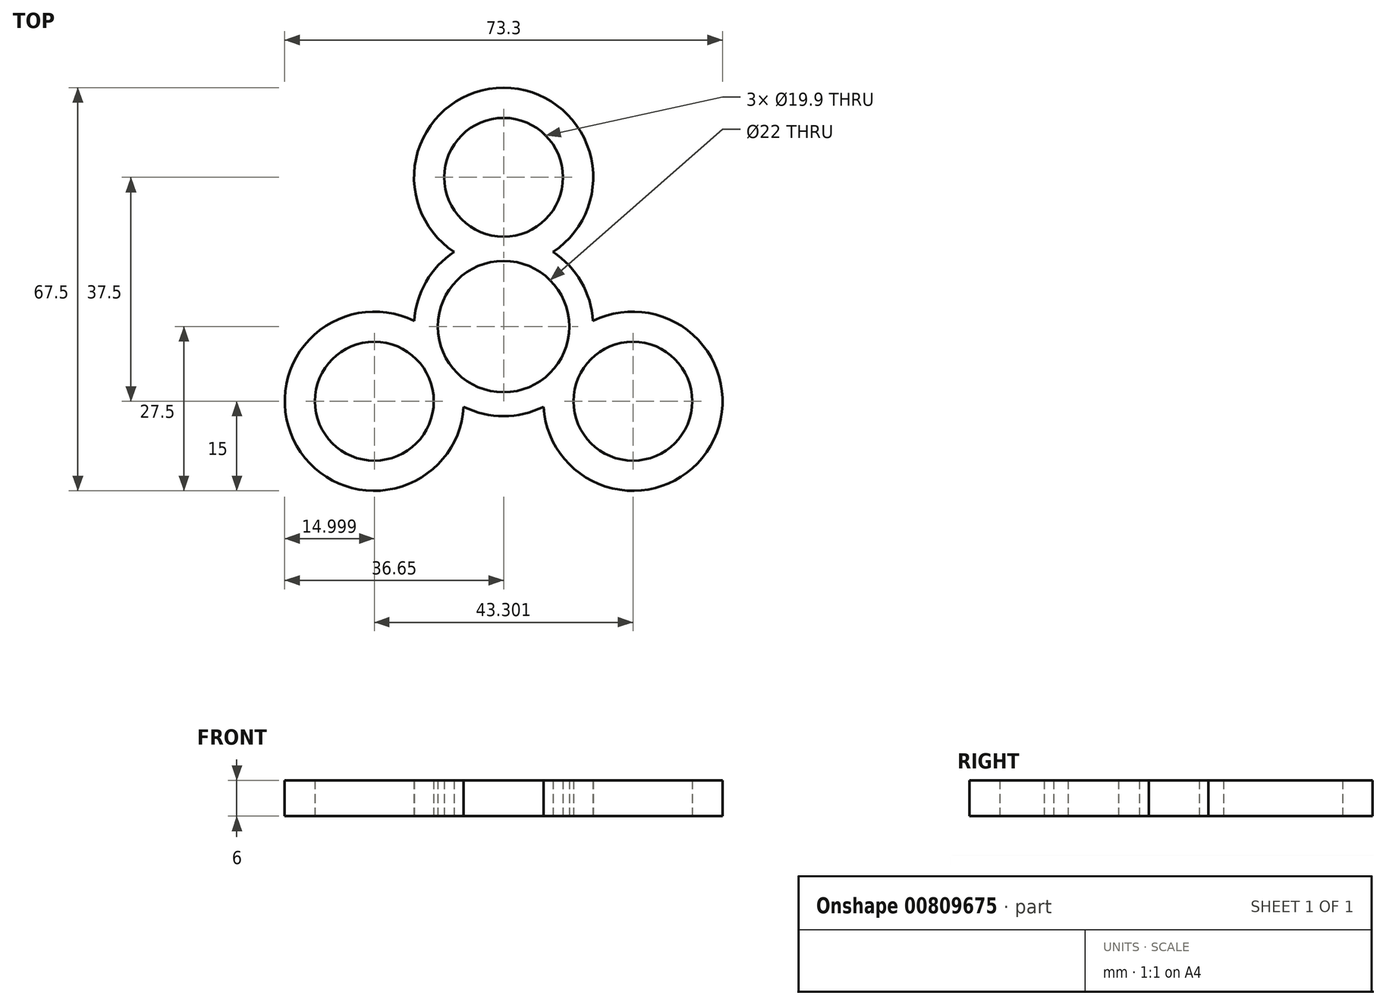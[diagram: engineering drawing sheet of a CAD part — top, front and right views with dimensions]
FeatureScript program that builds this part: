
annotation { "Feature Type Name" : "Feature", "Feature Type Description" : "" }
export const myFeature = defineFeature(function(context is Context, id is Id, definition is map)
    precondition{}
    {
        {
            var Q0;
            Q0=qCreatedBy(makeId("Top.planeOp"),FACE);
            var sketch = newSketch(context, id + "F0", { "sketchPlane" : qUnion([Q0])});
            skArc(sketch, "E0", {"start": v(9.53, 5.5) * mm, "mid": v(0, 11) * mm, "end": v(-9.53, 5.5) * mm});
            skCircle(sketch, "E1", {"center": v(0, 25) * mm, "radius": 9.95 * mm});
            skArc(sketch, "E2", {"start": v(-8.3, 12.5) * mm, "mid": v(-10.93, 10.27) * mm, "end": v(-13, 7.5) * mm});
            skArc(sketch, "E3", {"start": v(8.3, 12.5) * mm, "mid": v(0, 40) * mm, "end": v(-8.3, 12.5) * mm});
            skArc(sketch, "E4.trimOffspring", {"start": v(13, 7.5) * mm, "mid": v(10.93, 10.27) * mm, "end": v(8.3, 12.5) * mm});
            skArc(sketch, "E5.1.0", {"start": v(-14.97, 0.93) * mm, "mid": v(-34.64, -20) * mm, "end": v(-6.68, -13.43) * mm});
            skCircle(sketch, "E5.1.1", {"center": v(-21.65, -12.5) * mm, "radius": 9.95 * mm});
            skArc(sketch, "E5.1.2", {"start": v(-13, 7.5) * mm, "mid": v(-14.36, 4.33) * mm, "end": v(-14.97, 0.93) * mm});
            skArc(sketch, "E5.1.3", {"start": v(-6.68, -13.43) * mm, "mid": v(-3.43, -14.6) * mm, "end": v(0, -15) * mm});
            skArc(sketch, "E5.1.4", {"start": v(-9.53, 5.5) * mm, "mid": v(-9.53, -5.5) * mm, "end": v(0, -11) * mm});
            skArc(sketch, "E5.2.0", {"start": v(6.68, -13.43) * mm, "mid": v(34.64, -20) * mm, "end": v(14.97, 0.93) * mm});
            skCircle(sketch, "E5.2.1", {"center": v(21.65, -12.5) * mm, "radius": 9.95 * mm});
            skArc(sketch, "E5.2.2", {"start": v(0, -15) * mm, "mid": v(3.43, -14.6) * mm, "end": v(6.68, -13.43) * mm});
            skArc(sketch, "E5.2.3", {"start": v(14.97, 0.93) * mm, "mid": v(14.36, 4.33) * mm, "end": v(13, 7.5) * mm});
            skArc(sketch, "E5.2.4", {"start": v(0, -11) * mm, "mid": v(9.53, -5.5) * mm, "end": v(9.53, 5.5) * mm});
            skSolve(sketch);
        }
        {
            var Q0;
            Q0 = qSketchRegion(id + "F0", true);
            extrude(context, id + "F1", {"entities" : qUnion([Q0]), "depth" : 6 * mm, "offsetDistance" : 25 * mm});
        }
    });
